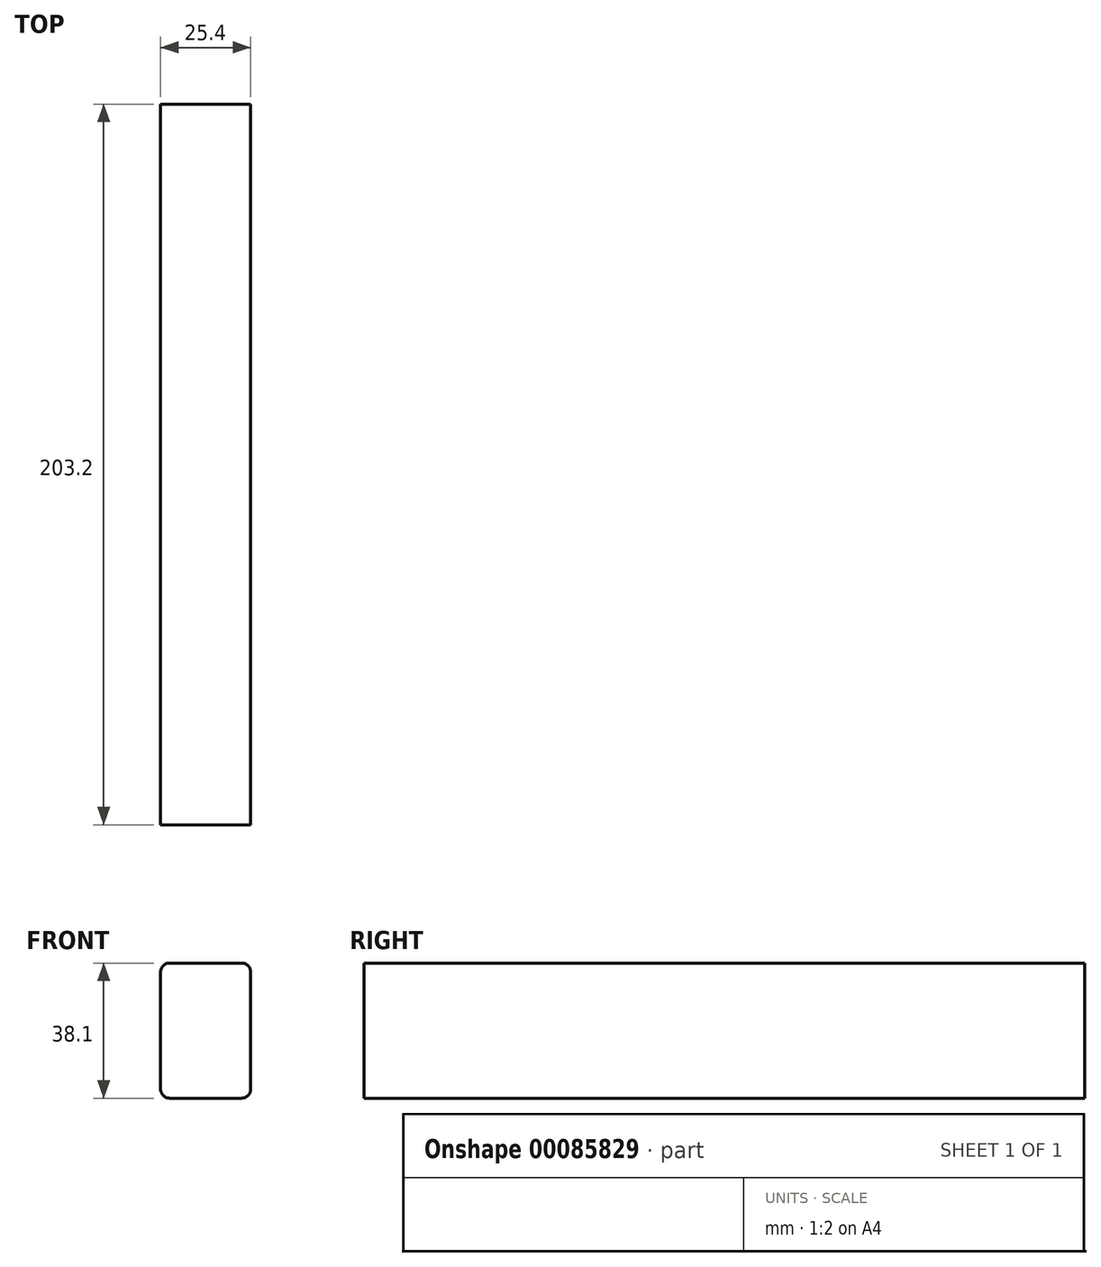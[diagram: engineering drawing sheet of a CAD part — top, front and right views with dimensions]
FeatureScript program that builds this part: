
annotation { "Feature Type Name" : "Feature", "Feature Type Description" : "" }
export const myFeature = defineFeature(function(context is Context, id is Id, definition is map)
    precondition{}
    {
        {
            var Q0;
            Q0=qCreatedBy(makeId("Front.planeOp"),FACE);
            var sketch = newSketch(context, id + "F0", { "sketchPlane" : qUnion([Q0])});
            skLineSegment(sketch, "E0.bottom", {"start": v(-42.09, 28.34) * mm, "end": v(-16.69, 28.34) * mm});
            skLineSegment(sketch, "E0.top", {"start": v(-42.09, -9.76) * mm, "end": v(-16.69, -9.76) * mm});
            skLineSegment(sketch, "E0.left", {"start": v(-42.09, 28.34) * mm, "end": v(-42.09, -9.76) * mm});
            skLineSegment(sketch, "E0.right", {"start": v(-16.69, 28.34) * mm, "end": v(-16.69, -9.76) * mm});
            skSolve(sketch);
        }
        {
            var Q0;
            Q0=makeQuery(id+"F0.imprint","IMPRINT",FACE,{"disambiguationData":[TD([[makeQuery(id+"F0.imprint","IMPRINT",EDGE,{"derivedFrom":sQuery(id+"F0.wireOp",EDGE,"E0.bottom")}),-1.0]])]});
            extrude(context, id + "F1", {"entities" : qUnion([Q0]), "depth" : 203.2 * mm, "offsetDistance" : 25.4 * mm});
        }
        {
            var Q0;
            Q0=makeQuery(id+"F1.opExtrude","SWEPT_EDGE",EDGE,{"disambiguationData":[OSD([sQuery(id+"F0.wireOp",EDGE,"E0.bottom"),sQuery(id+"F0.wireOp",EDGE,"E0.right")])]});
            var Q1;
            Q1=makeQuery(id+"F1.opExtrude","SWEPT_EDGE",EDGE,{"disambiguationData":[OSD([sQuery(id+"F0.wireOp",EDGE,"E0.bottom"),sQuery(id+"F0.wireOp",EDGE,"E0.left")])]});
            var Q2;
            Q2=makeQuery(id+"F1.opExtrude","SWEPT_EDGE",EDGE,{"disambiguationData":[OSD([sQuery(id+"F0.wireOp",EDGE,"E0.top"),sQuery(id+"F0.wireOp",EDGE,"E0.left")])]});
            var Q3;
            Q3=makeQuery(id+"F1.opExtrude","SWEPT_EDGE",EDGE,{"disambiguationData":[OSD([sQuery(id+"F0.wireOp",EDGE,"E0.top"),sQuery(id+"F0.wireOp",EDGE,"E0.right")])]});
            fillet(context, id + "F2", {"entities" : qUnion([Q0, Q1, Q2, Q3]), "radius" : 2.54 * mm, "tangentPropagation" : true, "allowEdgeOverflow" : false});
        }
    });
